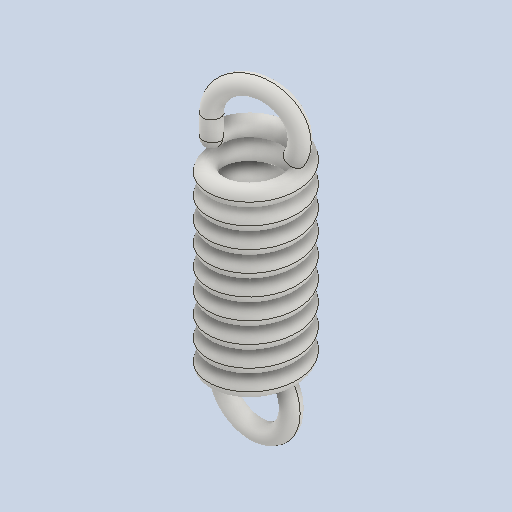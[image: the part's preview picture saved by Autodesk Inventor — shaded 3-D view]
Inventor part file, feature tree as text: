
AUTODESK INVENTOR PART (.ipt)
format: ipt  version: 2025 (Build 290162010, 162A)  size: 1,194,496 bytes
history: native  units: mm
features: sketch x97, plane x32, other x32, sweep x22, extrude x10, helix x4
ambient origin geometry x8: Origin, YZ Plane, XZ Plane, XY Plane, X Axis, Y Axis, Z Axis, Center Point
bodies: Solid1 (feature_tree)
feature tree (197):
  sketch  "3D Sketch2"
  plane  "ArbeitsebeneSweeping1"
  sweep  "Sweep1"
  other  "Erste Umdrehung mit Ösentyp 0(Rechts)"
  sketch  "Sketch8"  dims[d5=0.0mm d6=90.0deg d7=90.0deg d8=0.0mm d9=0.0mm d12=3.6mm]
  plane  "ArbeitsebeneExtrusion7"
  sketch  "Sketch10"  dims[d17=90.0deg d24=0.0mm d25=4.177895mm]
  plane  "ArbeitsebeneSweeping2"
  sweep  "Sweep2"
  other  "Zweite Umdrehung mit Ösentyp 0(Rechts)"
  sketch  "Sketch12"  dims[d26=10.0mm d27=90.476191mm]
  plane  "ArbeitsebeneExtrusion8"
  sketch  "Sketch110"  dims[d396=50.0mm]
  sketch  "3D Sketch20"
  plane  "ArbeitsebeneSweeping3"
  sweep  "Sweep3"
  sketch  "3D Sketch3"
  plane  "ArbeitsebeneSweeping6"
  sweep  "Sweep6"
  other  "Erste Umdrehung mit Ösentyp 0(Links)"
  sketch  "Sketch24"  dims[d171=0.0mm d172=90.0deg]
  plane  "ArbeitsebeneExtrusion5"
  sketch  "Sketch18"  dims[d86=90.0deg d87=20.0mm d90=20.0mm]
  plane  "ArbeitsebeneSweeping7"
  sweep  "Sweep7"
  other  "Zweite Umdrehung mit Ösentyp 0(Links)"
  sketch  "Sketch20"  dims[d149=90.0deg d152=20.0mm]
  plane  "ArbeitsebeneExtrusion6"
  sketch  "Sketch22"  dims[d169=300.0deg d170=4.775mm]
  plane  "ArbeitsebeneSweeping8"
  sweep  "Sweep8"
  other  "Erste Umdrehung mit Ösentyp 1(Links)"
  sketch  "Sketch27"  dims[d175=0.0mm d176=300.0deg]
  plane  "ArbeitsebeneExtrusion9"
  extrude  "Extrusion9"  Depth=10.0mm
  sketch  "Sketch29"  dims[d179=30.0mm d180=90.0deg]
  plane  "ArbeitsebeneSweeping9"
  sweep  "Sweep9"
  other  "Zweite Umdrehung mit Ösentyp 1(Links)"
  sketch  "Sketch32"  dims[d183=0.0mm d184=30.0mm d185=30.0mm d186=30.0mm]
  plane  "ArbeitsebeneExtrusion10"
  sketch  "Sketch34"  dims[d189=7.2mm d190=0.0mm]
  sketch  "3D Sketch22"
  plane  "ArbeitsebeneSweeping10"
  sweep  "Sweep10"
  other  "Erste Umdrehung mit Ösentyp 1(Rechts)"
  sketch  "Sketch42"  dims[d195=40.0mm d196=7.2mm]
  plane  "ArbeitsebeneExtrusion11"
  extrude  "Extrusion11"  Depth=20.0mm
  sketch  "Sketch44"  dims[d199=300.0deg d200=4.775mm]
  plane  "ArbeitsebeneSweeping11"
  sweep  "Sweep11"
  other  "Zweite Umdrehung mit Ösentyp 1(Rechts)"
  sketch  "Sketch112"  dims[d397=29.670597mm]
  plane  "ArbeitsebeneExtrusion12"
  sketch  "Sketch114"  dims[d401=50.0mm]
  sketch  "3D Sketch24"
  plane  "ArbeitsebeneSweeping12"
  sweep  "Sweep12"
  sketch  "Sketch46"  dims[d201=0.0mm d202=90.0deg]
  other  "Erstes Sweeping mit Ösentyp 2(Links)"
  sweep  "SweepingLinksÖse21"
  sketch  "Sketch48"  dims[d206=300.0deg d207=4.775mm]
  other  "Zweites Sweeping mit Ösentyp 2(Links)"
  sweep  "SweepingLinksÖse22"
  sketch  "Sketch50"  dims[d210=7.2mm d211=0.0mm d212=90.0deg d213=300.0deg d214=4.775mm]
  other  "Erstes Sweeping mit Ösentyp 2(Rechts)"
  sweep  "SweepingRechtsÖse21"
  sketch  "Sketch52"  dims[d220=50.0mm]
  other  "Zweites Sweeping mit Ösentyp 2(Rechts)"
  sweep  "SweepingRechtsÖse22"
  other  "Erste Umdrehung mit Ösentyp 3(Links)"
  extrude  "Extrusion1"  TaperAngle=90.0deg  [1 undecoded]
  sweep  "Sweep19"
  other  "Zweite Umdrehung mit Ösentyp 3(Links)"
  extrude  "Extrusion2"  Depth=30.0mm
  sketch  "Sketch60"  dims[d242=90.0deg]
  plane  "ArbeitsebeneSweeping20"
  sweep  "Sweep20"
  other  "Erste Umdrehung mit Ösentyp 3(Rechts)"
  extrude  "Extrusion3"  TaperAngle=0.0deg  [1 undecoded]
  sweep  "Sweep21"
  other  "Zweite Umdrehung mit Ösentyp 3(Rechts)"
  extrude  "Extrusion4"  TaperAngle=90.0deg  [1 undecoded]
  sketch  "Sketch68"  dims[d282=60.0mm]
  plane  "Work Plane46"
  sweep  "Sweep22"
  other  "Erste Umdrehung mit Ösentyp 4(Links)"
  sketch  "Sketch71"  dims[d301=10.0mm d302=15.0mm d303=0.0mm d304=90.0deg d305=90.0deg d306=0.0mm d307=0.0mm]
  plane  "ArbeitsebeneExtrusion13"
  extrude  "Extrusion13"  TaperAngle=90.0deg  [1 undecoded]
  sketch  "Sketch73"  dims[d310=4.1mm]
  plane  "ArbeitsebeneSweeping23"
  sweep  "Sweep23"
  other  "Zweite Umdrehung mit Ösentyp 4(Links)"
  sketch  "Sketch76"  dims[d320=5.675mm]
  plane  "ArbeitsebeneExtrusion14"
  sketch  "Sketch78"  dims[d322=10.0mm d323=15.0mm d324=0.0mm d325=90.0deg d326=90.0deg d327=0.0mm d328=0.0mm d329=70.0mm]
  sketch  "3D Sketch26"
  plane  "ArbeitsebeneSweeping24"
  sweep  "Sweep24"
  other  "Erste Umdrehung mit Ösentyp 4(Rechts)"
  sketch  "Sketch86"  dims[d332=10.0mm d333=15.0mm d334=0.0mm d335=90.0deg d336=90.0deg d337=0.0mm d338=0.0mm d339=70.0mm]
  plane  "Work PlaneExtrusion15"
  extrude  "Extrusion15"  Depth=7.2mm TaperAngle=0.0deg
  sketch  "Sketch88"  dims[d361=10.0mm]
  plane  "ArbeitsebeneSweeping25"
  sweep  "Sweep25"
  other  "Zweite Umdrehung mit Ösentyp 4(Rechts)"
  sketch  "Sketch116"  dims[d404=4.15mm]
  plane  "ArbeitsebeneExtrusion16"
  sketch  "Sketch118"  dims[d406=50.0mm d407=29.670597mm d408=0.0mm d411=60.0mm d423=60.0mm d433=4.15mm d434=0.0mm d435=4.775mm d436=4.1mm d437=10.0mm d438=15.0mm d439=0.0mm d440=90.0deg d441=90.0deg d442=0.0mm d443=0.0mm d444=60.0mm d447=60.0mm d457=4.15mm d458=0.0mm d459=60.0mm d469=90.0deg d478=90.0deg d479=4.775mm d480=4.1mm d481=25.4mm d482=15.0mm d483=0.0mm d484=90.0deg d485=90.0deg d486=0.0mm d487=0.0mm d491=10.0mm d498=10.0mm d501=0.0mm d502=4.15mm d503=0.0mm d504=210.0deg d505=0.0mm d506=0.0mm d507=4.15mm d508=0.0mm d509=29.670597mm d510=0.0mm d511=10.0mm d512=0.0mm d513=4.15mm d514=0.0mm d515=29.670597mm d516=0.0mm d517=0.0mm d518=4.15mm d519=0.0mm d520=4.775mm d521=4.1mm d522=10.0mm d523=15.0mm d524=0.0mm d525=90.0deg d526=90.0deg d527=0.0mm d528=0.0mm d529=60.0mm d530=50.0mm d531=0.0mm d532=4.15mm d533=0.0mm d534=20.0mm d535=210.0deg d536=0.0mm d537=0.0mm d538=4.15mm d539=0.0mm d540=29.670597mm d541=0.0mm d542=50.0mm d543=0.0mm d544=4.15mm d545=0.0mm d546=60.0mm d547=4.775mm d548=4.1mm d549=10.0mm d550=15.0mm d551=0.0mm d552=90.0deg d553=90.0deg d554=0.0mm d555=0.0mm d561=10.0mm d564=0.0mm d565=4.15mm d566=0.0mm d567=10.0mm d569=29.670597mm d570=0.0mm d571=90.0deg d578=0.0mm d579=3.6mm d580=4.15mm d581=0.0mm d584=10.0mm d585=10.0mm d588=29.670597mm d589=0.0mm d590=0.0mm d591=0.0mm d592=0.0mm d593=0.0mm d594=0.0mm d595=0.0mm d596=0.0mm d597=0.0mm d598=0.0mm d599=0.0mm d600=0.0mm d601=0.0mm d602=0.0mm d603=0.0mm d604=0.0mm d605=0.0mm d606=0.0mm d607=0.0mm d608=0.0mm d609=0.0mm d610=0.0mm d611=0.0mm]
  sketch  "3D Sketch28"
  plane  "ArbeitsebeneSweeping26"
  sweep  "Sweep26"
  other  "Erste Umdrehung mit Ösentyp 5(Links)"
  sketch  "Sketch91"  dims[d365=0.0mm]
  plane  "ArbeitsebeneExtrusion17"
  extrude  "Extrusion17"  TaperAngle=0.0deg  [1 undecoded]
  helix  "Coil1"  [1 undecoded]
  other  "Zweite Umdrehung mit Ösentyp 5(Links)"
  sketch  "Sketch95"  dims[d373=20.0mm]
  plane  "ArbeitsebeneExtrusion18"
  helix  "Coil2"  [1 undecoded]
  other  "Erste Umdrehung mit Ösentyp 5(Rechts)"
  sketch  "Sketch99"  dims[d377=210.0deg]
  plane  "ArbeitsebeneExtrusion19"
  helix  "Coil13"  [1 undecoded]
  other  "Zweite Umdrehung mit Ösentyp 5(Rechts)"
  sketch  "Sketch103"  dims[d385=0.0mm]
  plane  "ArbeitsebeneExtrusion20"
  extrude  "Extrusion20"  Depth=40.0mm
  sketch  "Sketch105"  dims[d387=210.0deg]
  helix  "Coil4"  [1 undecoded]
  other  "Erste Spirale mit Ösentyp 6(Links)"
  other  "Zweite Spirale mit Ösentyp 6(Links)"
  other  "Erste Spirale mit Ösentyp 6(Rechts)"
  other  "Zweite Spirale mit Ösentyp 6(Rechts)"
  other  "Srf1"
  sketch  "Sketch4"  dims[d0=0.9mm d1=7.2mm]
  sketch  "Sketch7"  dims[d2=4.177895mm d3=10.0mm d4=90.476191mm]
  other  "Srf2"
  sketch  "Sketch16"  dims[d38=90.0deg d54=10.0mm d55=10.0mm]
  sketch  "Sketch26"  dims[d173=300.0deg d174=4.775mm]
  sketch  "Sketch31"  dims[d181=300.0deg d182=5.675mm]
  sketch  "Sketch36"  dims[d191=300.0deg d192=4.775mm]
  sketch  "Sketch41"  dims[d193=0.0mm d194=90.0deg]
  sketch  "Sketch47"  dims[d203=40.0mm d204=7.2mm d205=0.0mm]
  sketch  "Sketch49"  dims[d208=0.0mm d209=90.0deg]
  sketch  "Sketch51"  dims[d215=0.0mm d216=40.0mm d217=90.0deg]
  sketch  "Sketch53"  dims[d223=90.0deg]
  sketch  "Sketch54"  dims[d226=50.0mm]
  sketch  "Sketch55"  dims[d229=90.0deg]
  sketch  "Sketch56"  dims[d232=50.0mm]
  sketch  "Sketch58"  dims[d235=90.0deg]
  sketch  "Sketch59"  dims[d238=50.0mm]
  sketch  "Sketch61"  dims[d243=60.0mm]
  sketch  "Sketch62"  dims[d255=90.0deg]
  sketch  "Sketch63"  dims[d256=60.0mm]
  sketch  "Sketch64"  dims[d268=90.0deg]
  sketch  "Sketch66"  dims[d269=60.0mm]
  sketch  "Sketch67"  dims[d281=90.0deg]
  sketch  "Sketch69"  dims[d299=5.675mm]
  sketch  "Sketch70"  dims[d300=4.1mm]
  sketch  "Sketch75"  dims[d311=10.0mm d312=15.0mm d313=0.0mm d314=90.0deg d315=90.0deg d316=0.0mm d317=0.0mm d318=70.0mm d319=70.0mm]
  sketch  "Sketch80"  dims[d330=5.675mm]
  sketch  "Sketch85"  dims[d331=4.1mm]
  sketch  "Sketch90"  dims[d364=4.15mm]
  sketch  "Sketch94"  dims[d368=0.0mm]
  sketch  "Sketch98"  dims[d376=20.0mm]
  sketch  "Sketch102"  dims[d384=4.15mm]
  sketch  "Sketch106"  dims[d388=0.0mm]
  sketch  "Sketch107"  dims[d391=50.0mm]
  sketch  "Sketch108"  dims[d394=4.15mm]
  sketch  "Sketch109"  dims[d395=0.0mm]
  sketch  "Sketch13"  dims[d28=0.0mm d29=90.0deg d30=90.0deg d31=0.0mm d32=0.0mm d33=3.6mm]
  sketch  "Sketch33"  dims[d187=90.0deg d188=40.0mm]
  sketch  "Sketch113"  dims[d398=0.0mm]
  sketch  "Sketch77"  dims[d321=4.1mm]
  sketch  "Sketch117"  dims[d405=0.0mm]
  sketch  "Sketch96"  dims[d374=4.15mm]
  sketch  "Sketch97"  dims[d375=0.0mm]
  sketch  "Sketch104"  dims[d386=20.0mm]
  sketch  "Sketch43"  dims[d197=0.0mm d198=90.0deg]
  sketch  "Sketch9"  dims[d13=0.0mm d14=90.0deg]
  sketch  "Sketch87"  dims[d350=10.0mm d352=10.0mm d353=10.0mm d356=10.0mm]
  sketch  "Sketch100"  dims[d378=0.0mm]
  sketch  "Sketch101"  dims[d381=20.0mm]
  sketch  "Sketch28"  dims[d177=5.675mm d178=0.0mm]
  sketch  "Sketch72"  dims[d308=5.675mm]
  sketch  "Sketch92"  dims[d366=10.0mm]
  sketch  "Sketch93"  dims[d367=29.670597mm]
  sketch  "Sketch21"  dims[d155=90.0deg d156=20.0mm]
  sketch  "Sketch15"  dims[d34=0.0mm d36=0.0mm]
  sketch  "Sketch17"  dims[d72=0.0mm d73=0.0mm d79=90.0deg]
  other  "Basisschraube(Rechts)"
  other  "Basisschraube(Links)"
note: 9 required parameter values undecoded (feature->parameter linkage not recoverable at this tier; creation-order binding heuristic only, values carry confidence <= 0.55)
